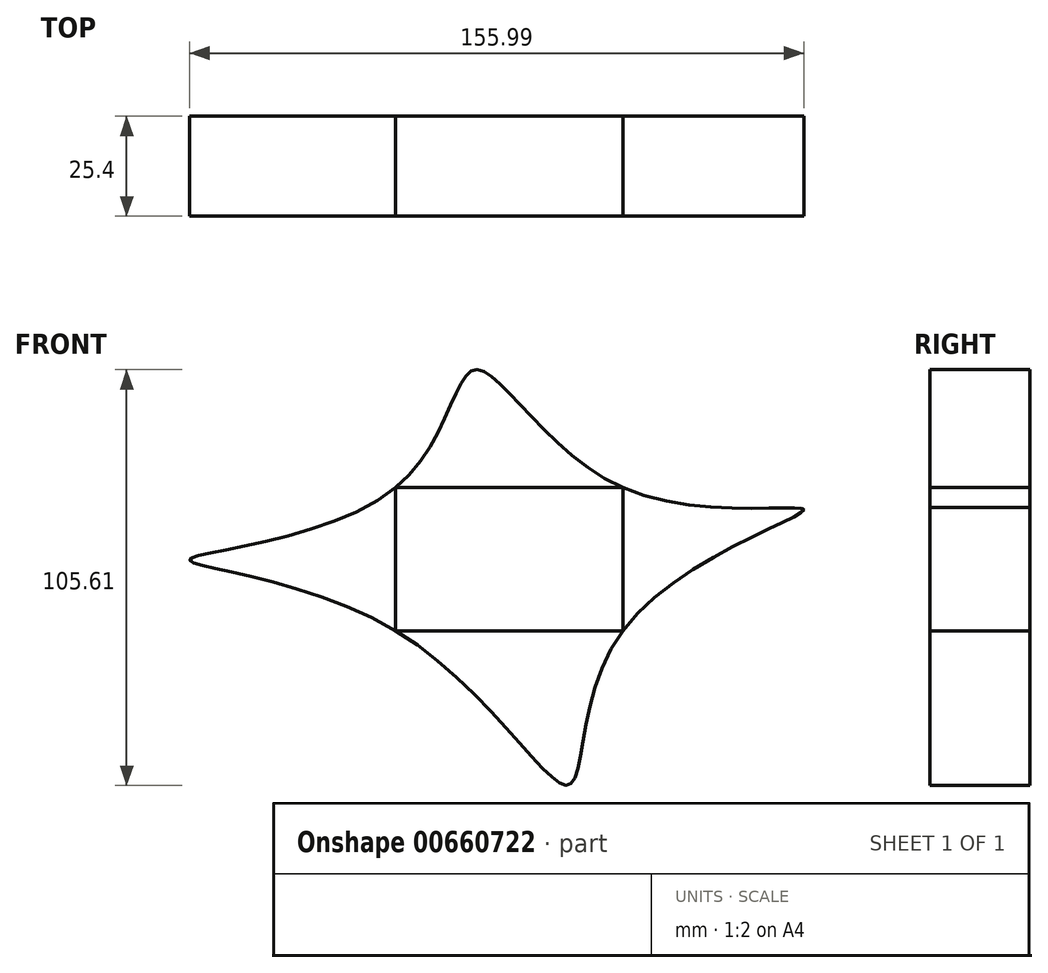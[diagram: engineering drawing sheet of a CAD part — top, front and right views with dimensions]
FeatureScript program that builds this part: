
annotation { "Feature Type Name" : "Feature", "Feature Type Description" : "" }
export const myFeature = defineFeature(function(context is Context, id is Id, definition is map)
    precondition{}
    {
        {
            var Q0;
            Q0=qCreatedBy(makeId("Front.planeOp"),FACE);
            var sketch = newSketch(context, id + "F0", { "sketchPlane" : qUnion([Q0])});
            skLineSegment(sketch, "E0", {"start": v(0, 0) * mm, "end": v(-57.74, 0) * mm});
            skLineSegment(sketch, "E1", {"start": v(-57.74, 0) * mm, "end": v(-57.74, 36.36) * mm});
            skLineSegment(sketch, "E2", {"start": v(-57.74, 36.36) * mm, "end": v(0, 36.36) * mm});
            skLineSegment(sketch, "E3", {"start": v(0, 36.36) * mm, "end": v(0, 0) * mm});
            skFitSpline(sketch, "E4", {"points": [v(-57.74, 36.36) * mm, v(-37.5, 66.31) * mm, v(0, 36.36) * mm, v(45.96, 30.72) * mm, v(0, 0) * mm, v(-13.7, -39.17) * mm, v(-57.74, 0) * mm, v(-109.97, 18.18) * mm, v(-57.74, 36.36) * mm]});
            skSolve(sketch);
        }
        {
            var Q0;
            {var subQ0=sQuery(id+"F0.wireOp",EDGE,"E0");Q0=makeQuery(id+"F0.imprint","IMPRINT",FACE,{"disambiguationData":[TD([[makeQuery(id+"F0.imprint","IMPRINT",EDGE,{"derivedFrom":subQ0}),1.0]])]});}
            var Q1;
            {var subQ0=sQuery(id+"F0.wireOp",EDGE,"E1");Q1=makeQuery(id+"F0.imprint","IMPRINT",FACE,{"disambiguationData":[TD([[makeQuery(id+"F0.imprint","IMPRINT",EDGE,{"derivedFrom":subQ0}),1.0]])]});}
            var Q2;
            {var subQ0=sQuery(id+"F0.wireOp",EDGE,"E2");Q2=makeQuery(id+"F0.imprint","IMPRINT",FACE,{"disambiguationData":[TD([[makeQuery(id+"F0.imprint","IMPRINT",EDGE,{"derivedFrom":subQ0}),1.0]])]});}
            var Q3;
            {var subQ0=sQuery(id+"F0.wireOp",EDGE,"E3");Q3=makeQuery(id+"F0.imprint","IMPRINT",FACE,{"disambiguationData":[TD([[makeQuery(id+"F0.imprint","IMPRINT",EDGE,{"derivedFrom":subQ0}),1.0]])]});}
            extrude(context, id + "F1", {"entities" : qUnion([Q0, Q1, Q2, Q3]), "depth" : 25.4 * mm, "offsetDistance" : 25.4 * mm});
        }
    });
